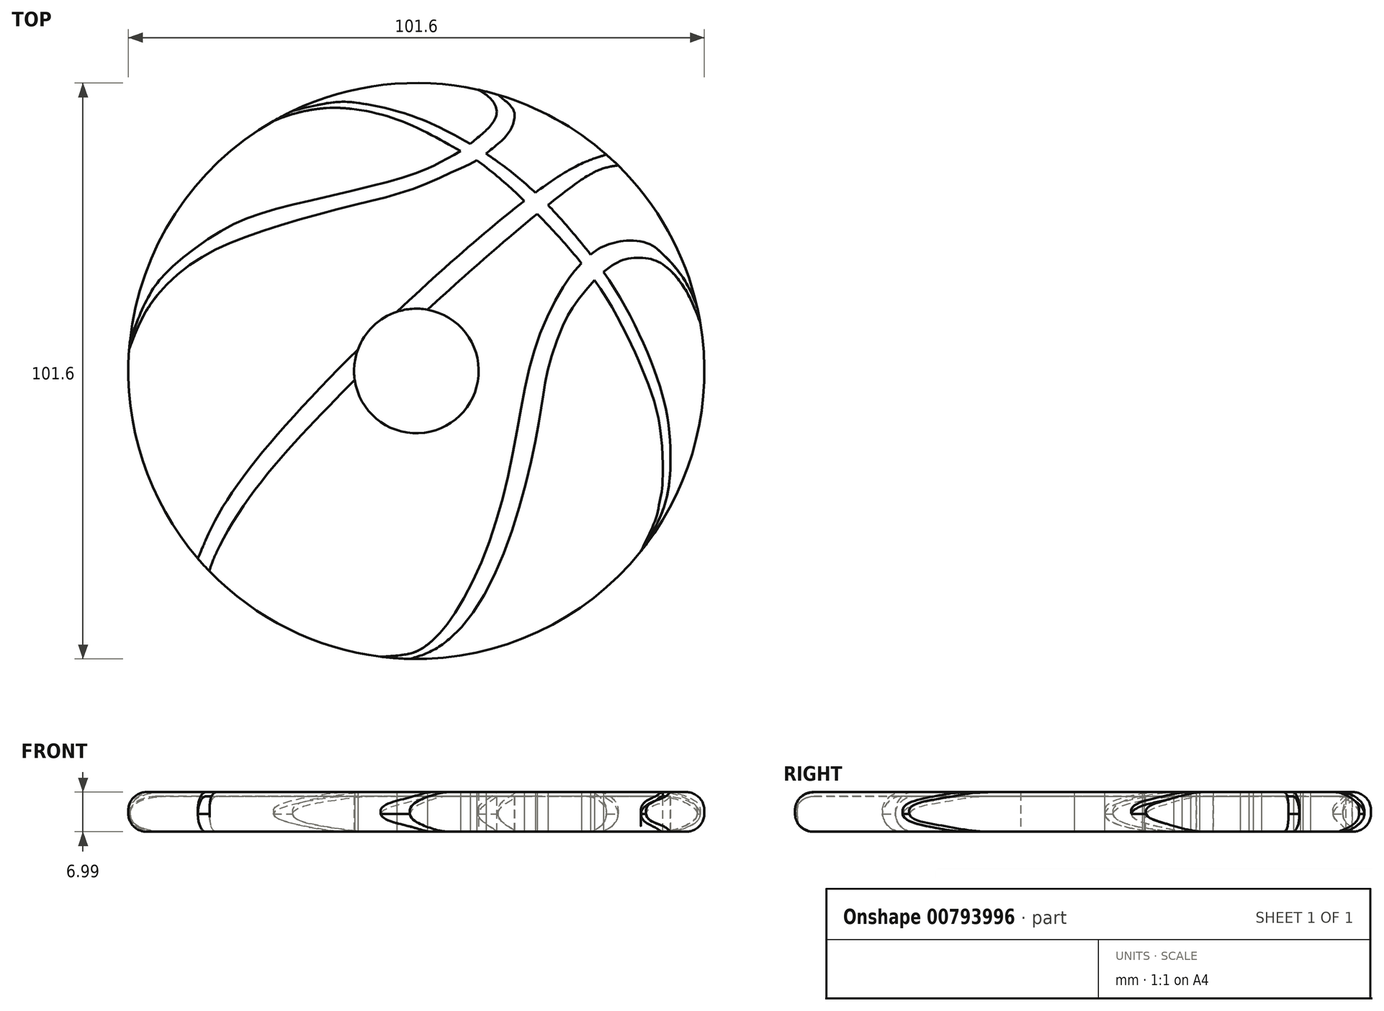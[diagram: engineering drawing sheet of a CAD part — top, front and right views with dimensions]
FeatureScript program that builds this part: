
annotation { "Feature Type Name" : "Feature", "Feature Type Description" : "" }
export const myFeature = defineFeature(function(context is Context, id is Id, definition is map)
    precondition{}
    {
        {
            var Q0;
            Q0=qCreatedBy(makeId("Top.planeOp"),FACE);
            var sketch = newSketch(context, id + "F0", { "sketchPlane" : qUnion([Q0])});
            skCircle(sketch, "E0", {"center": v(0, 0) * mm, "radius": 10.99 * mm});
            skCircle(sketch, "E1", {"center": v(0, 0) * mm, "radius": 50.8 * mm});
            skFitSpline(sketch, "E2", {"points": [v(-38.55, -33.09) * mm, v(-32.94, -22.07) * mm, v(-12.55, 1.56) * mm, v(15.88, 27.48) * mm, v(28.35, 36.2) * mm, v(33.51, 38.18) * mm], "startDerivative": vector(26.52, 63.02) * mm, "endDerivative": vector(44.22, 13.53) * mm});
            skFitSpline(sketch, "E3", {"points": [v(35.58, 36.26) * mm, v(33.47, 35.87) * mm, v(28.86, 33.55) * mm, v(2.6, 11.4) * mm, v(-14.88, -5.64) * mm, v(-31.38, -25.11) * mm, v(-36.45, -35.38) * mm, v(-36.28, -35.56) * mm], "startDerivative": vector(-32.77, -4.24) * mm, "endDerivative": vector(11.2, -3.56) * mm});
            skFitSpline(sketch, "E4", {"points": [v(-50.66, 3.83) * mm, v(-47.23, 11.26) * mm, v(-40.15, 18.58) * mm, v(-29.32, 23.93) * mm, v(-12.42, 28.9) * mm, v(-0.95, 32) * mm, v(6.94, 35.36) * mm, v(10.57, 37.12) * mm, v(12.84, 38.78) * mm, v(15.6, 41.18) * mm, v(16.88, 43.13) * mm, v(17.35, 45.02) * mm, v(16.87, 46.44) * mm, v(14.4, 48.72) * mm], "startDerivative": vector(30.71, 83.36) * mm, "endDerivative": vector(-51.21, 39.87) * mm});
            skFitSpline(sketch, "E5", {"points": [v(10.85, 49.63) * mm, v(12.98, 48.15) * mm, v(14.02, 46.6) * mm, v(14.1, 45.01) * mm, v(12.56, 42.7) * mm, v(9.65, 40.22) * mm, v(7.47, 38.59) * mm, v(4.88, 37.2) * mm, v(2.28, 35.85) * mm, v(-5.69, 33.19) * mm, v(-23.58, 28.89) * mm, v(-33.83, 25.05) * mm, v(-42.81, 18.58) * mm, v(-46.8, 13.9) * mm, v(-49.27, 8.7) * mm, v(-50.53, 5.27) * mm], "startDerivative": vector(49.03, -27.61) * mm, "endDerivative": vector(-19.2, -56.5) * mm});
            skFitSpline(sketch, "E6", {"points": [v(-25.25, 44.08) * mm, v(-21.6, 45.38) * mm, v(-16.31, 46.34) * mm, v(-11.02, 46.2) * mm, v(-4.62, 44.77) * mm, v(1.88, 42.02) * mm, v(6.9, 39.3) * mm, v(11.36, 36.64) * mm, v(16, 32.85) * mm, v(18.05, 30.97) * mm, v(23.06, 25.9) * mm, v(27.84, 20.58) * mm, v(33.1, 13.56) * mm, v(37.68, 5.17) * mm, v(40.4, -1.03) * mm, v(42.45, -7.23) * mm, v(43.42, -14.55) * mm, v(43.34, -20.68) * mm, v(42.78, -23.76) * mm, v(42.38, -25.61) * mm, v(40.73, -29.53) * mm, v(39.6, -31.82) * mm, v(39.61, -31.8) * mm], "startDerivative": vector(85.9, 34.36) * mm, "endDerivative": vector(5.21, 7.59) * mm});
            skFitSpline(sketch, "E7", {"points": [v(40.48, -30.69) * mm, v(41.8, -28.23) * mm, v(43.88, -23.43) * mm, v(44.82, -16.64) * mm, v(44.28, -8.22) * mm, v(41.16, 2.27) * mm, v(33.84, 16.28) * mm, v(27.1, 24.95) * mm, v(23.82, 28.63) * mm, v(16.07, 35.65) * mm, v(4.58, 42.74) * mm, v(-3.48, 45.87) * mm, v(-8.9, 47.06) * mm, v(-15.22, 47.32) * mm, v(-21.87, 45.85) * mm, v(-21.82, 45.87) * mm], "startDerivative": vector(30.28, 53.24) * mm, "endDerivative": vector(13.66, 5.99) * mm});
            skFitSpline(sketch, "E8", {"points": [v(50.08, 8.51) * mm, v(48.7, 11.91) * mm, v(47.22, 14.73) * mm, v(45.05, 17.48) * mm, v(42.78, 19.2) * mm, v(40.3, 19.93) * mm, v(37.19, 19.77) * mm, v(34.29, 18.44) * mm, v(30.3, 14.76) * mm, v(27.7, 11.31) * mm, v(26.2, 8.77) * mm, v(23.46, 1.25) * mm, v(22.42, -3.96) * mm, v(21.18, -11.48) * mm, v(16.87, -28.15) * mm, v(9.65, -43.12) * mm, v(3.23, -49.1) * mm, v(-1.14, -50.79) * mm], "startDerivative": vector(-27.86, 72.87) * mm, "endDerivative": vector(-78.57, -22.07) * mm});
            skFitSpline(sketch, "E9", {"points": [v(-6.28, -50.41) * mm, v(-2.71, -50.13) * mm, v(0.45, -49.27) * mm, v(3.49, -46.92) * mm, v(6.26, -43.54) * mm, v(11.48, -33.71) * mm, v(16.31, -17.9) * mm, v(19.39, -2) * mm, v(22.68, 8.65) * mm, v(26.66, 16.05) * mm, v(28.24, 17.97) * mm, v(31.15, 20.88) * mm, v(33.92, 22.33) * mm, v(37.05, 22.98) * mm, v(41.06, 22.42) * mm, v(43.42, 20.67) * mm, v(45.13, 18.91) * mm, v(47, 16.48) * mm, v(48.5, 13.78) * mm, v(49.58, 11.09) * mm, v(49.6, 10.98) * mm], "startDerivative": vector(83, 3.39) * mm, "endDerivative": vector(1.21, -9.03) * mm});
            skSolve(sketch);
        }
        {
            var Q0;
            {var subQ0=sQuery(id+"F0.wireOp",EDGE,"E4");var subQ1=sQuery(id+"F0.wireOp",EDGE,"E1");var subQ2=makeQuery(id+"F0.imprint","INTERSECT",VERTEX,{"disambiguationData":[OD(0.0)],"derivedFrom":[subQ1,subQ0]});Q0=makeQuery(id+"F0.imprint","IMPRINT",FACE,{"disambiguationData":[TD([[makeQuery(id+"F0.imprint","IMPRINT",EDGE,{"disambiguationData":[TD([[subQ2,1.0]])],"derivedFrom":subQ1}),1.0]])]});}
            var Q1;
            {var subQ0=sQuery(id+"F0.wireOp",EDGE,"E6");var subQ1=sQuery(id+"F0.wireOp",EDGE,"E4");var subQ2=makeQuery(id+"F0.imprint","INTERSECT",VERTEX,{"derivedFrom":[subQ1,subQ0]});Q1=makeQuery(id+"F0.imprint","IMPRINT",FACE,{"disambiguationData":[TD([[makeQuery(id+"F0.imprint","IMPRINT",EDGE,{"disambiguationData":[TD([[subQ2,-1.0]])],"derivedFrom":subQ1}),1.0]])]});}
            var Q2;
            {var subQ0=sQuery(id+"F0.wireOp",EDGE,"E4");var subQ1=sQuery(id+"F0.wireOp",EDGE,"E1");var subQ2=makeQuery(id+"F0.imprint","INTERSECT",VERTEX,{"disambiguationData":[OD(1.0)],"derivedFrom":[subQ1,subQ0]});Q2=makeQuery(id+"F0.imprint","IMPRINT",FACE,{"disambiguationData":[TD([[makeQuery(id+"F0.imprint","IMPRINT",EDGE,{"disambiguationData":[TD([[subQ2,-1.0]])],"derivedFrom":subQ1}),1.0]])]});}
            var Q3;
            {var subQ0=sQuery(id+"F0.wireOp",EDGE,"E6");var subQ1=sQuery(id+"F0.wireOp",EDGE,"E1");var subQ2=makeQuery(id+"F0.imprint","INTERSECT",VERTEX,{"disambiguationData":[OD(0.0)],"derivedFrom":[subQ1,subQ0]});Q3=makeQuery(id+"F0.imprint","IMPRINT",FACE,{"disambiguationData":[TD([[makeQuery(id+"F0.imprint","IMPRINT",EDGE,{"disambiguationData":[TD([[subQ2,1.0]])],"derivedFrom":subQ1}),1.0]])]});}
            var Q4;
            {var subQ0=sQuery(id+"F0.wireOp",EDGE,"E6");var subQ1=sQuery(id+"F0.wireOp",EDGE,"E2");var subQ2=makeQuery(id+"F0.imprint","INTERSECT",VERTEX,{"derivedFrom":[subQ1,subQ0]});Q4=makeQuery(id+"F0.imprint","IMPRINT",FACE,{"disambiguationData":[TD([[makeQuery(id+"F0.imprint","IMPRINT",EDGE,{"disambiguationData":[TD([[subQ2,-1.0]])],"derivedFrom":subQ1}),1.0]])]});}
            var Q5;
            {var subQ0=sQuery(id+"F0.wireOp",EDGE,"E6");var subQ1=sQuery(id+"F0.wireOp",EDGE,"E2");var subQ2=makeQuery(id+"F0.imprint","INTERSECT",VERTEX,{"derivedFrom":[subQ1,subQ0]});Q5=makeQuery(id+"F0.imprint","IMPRINT",FACE,{"disambiguationData":[TD([[makeQuery(id+"F0.imprint","IMPRINT",EDGE,{"disambiguationData":[TD([[subQ2,-1.0]])],"derivedFrom":subQ1}),-1.0]])]});}
            var Q6;
            {var subQ0=sQuery(id+"F0.wireOp",EDGE,"E2");var subQ1=sQuery(id+"F0.wireOp",EDGE,"E1");var subQ2=makeQuery(id+"F0.imprint","INTERSECT",VERTEX,{"disambiguationData":[OD(1.0)],"derivedFrom":[subQ1,subQ0]});Q6=makeQuery(id+"F0.imprint","IMPRINT",FACE,{"disambiguationData":[TD([[makeQuery(id+"F0.imprint","IMPRINT",EDGE,{"disambiguationData":[TD([[subQ2,1.0]])],"derivedFrom":subQ1}),1.0]])]});}
            var Q7;
            {var subQ0=sQuery(id+"F0.wireOp",EDGE,"E2");var subQ1=sQuery(id+"F0.wireOp",EDGE,"E0");var subQ2=makeQuery(id+"F0.imprint","INTERSECT",VERTEX,{"disambiguationData":[OD(0.0)],"derivedFrom":[subQ1,subQ0]});Q7=makeQuery(id+"F0.imprint","IMPRINT",FACE,{"disambiguationData":[TD([[makeQuery(id+"F0.imprint","IMPRINT",EDGE,{"disambiguationData":[TD([[subQ2,1.0]])],"derivedFrom":subQ1}),-1.0]])]});}
            var Q8;
            {var subQ0=sQuery(id+"F0.wireOp",EDGE,"E2");var subQ1=sQuery(id+"F0.wireOp",EDGE,"E0");var subQ2=makeQuery(id+"F0.imprint","INTERSECT",VERTEX,{"disambiguationData":[OD(1.0)],"derivedFrom":[subQ1,subQ0]});Q8=makeQuery(id+"F0.imprint","IMPRINT",FACE,{"disambiguationData":[TD([[makeQuery(id+"F0.imprint","IMPRINT",EDGE,{"disambiguationData":[TD([[subQ2,-1.0]])],"derivedFrom":subQ1}),-1.0]])]});}
            var Q9;
            {var subQ0=sQuery(id+"F0.wireOp",EDGE,"E8");var subQ1=sQuery(id+"F0.wireOp",EDGE,"E1");var subQ2=makeQuery(id+"F0.imprint","INTERSECT",VERTEX,{"disambiguationData":[OD(1.0)],"derivedFrom":[subQ1,subQ0]});Q9=makeQuery(id+"F0.imprint","IMPRINT",FACE,{"disambiguationData":[TD([[makeQuery(id+"F0.imprint","IMPRINT",EDGE,{"disambiguationData":[TD([[subQ2,1.0]])],"derivedFrom":subQ1}),1.0]])]});}
            var Q10;
            {var subQ0=sQuery(id+"F0.wireOp",EDGE,"E7");var subQ1=sQuery(id+"F0.wireOp",EDGE,"E3");var subQ2=makeQuery(id+"F0.imprint","INTERSECT",VERTEX,{"derivedFrom":[subQ1,subQ0]});Q10=makeQuery(id+"F0.imprint","IMPRINT",FACE,{"disambiguationData":[TD([[makeQuery(id+"F0.imprint","IMPRINT",EDGE,{"disambiguationData":[TD([[subQ2,-1.0]])],"derivedFrom":subQ1}),1.0]])]});}
            var Q11;
            {var subQ0=sQuery(id+"F0.wireOp",EDGE,"E9");var subQ1=sQuery(id+"F0.wireOp",EDGE,"E6");var subQ2=makeQuery(id+"F0.imprint","INTERSECT",VERTEX,{"derivedFrom":[subQ1,subQ0]});Q11=makeQuery(id+"F0.imprint","IMPRINT",FACE,{"disambiguationData":[TD([[makeQuery(id+"F0.imprint","IMPRINT",EDGE,{"disambiguationData":[TD([[subQ2,-1.0]])],"derivedFrom":subQ1}),1.0]])]});}
            var Q12;
            {var subQ0=sQuery(id+"F0.wireOp",EDGE,"E8");var subQ1=sQuery(id+"F0.wireOp",EDGE,"E1");var subQ2=makeQuery(id+"F0.imprint","INTERSECT",VERTEX,{"disambiguationData":[OD(0.0)],"derivedFrom":[subQ1,subQ0]});Q12=makeQuery(id+"F0.imprint","IMPRINT",FACE,{"disambiguationData":[TD([[makeQuery(id+"F0.imprint","IMPRINT",EDGE,{"disambiguationData":[TD([[subQ2,-1.0]])],"derivedFrom":subQ1}),1.0]])]});}
            var Q13;
            {var subQ1=sQuery(id+"F0.wireOp",EDGE,"E1");var subQ5=sQuery(id+"F0.wireOp",EDGE,"E6");var subQ8=makeQuery(id+"F0.imprint","INTERSECT",VERTEX,{"disambiguationData":[OD(1.0)],"derivedFrom":[subQ1,subQ5]});Q13=makeQuery(id+"F0.imprint","IMPRINT",FACE,{"disambiguationData":[TD([[makeQuery(id+"F0.imprint","IMPRINT",EDGE,{"disambiguationData":[TD([[subQ8,1.0]])],"derivedFrom":subQ1}),1.0]])]});}
            extrude(context, id + "F1", {"entities" : qUnion([Q0, Q1, Q2, Q3, Q4, Q5, Q6, Q7, Q8, Q9, Q10, Q11, Q12, Q13]), "depth" : 6.22 * mm, "offsetDistance" : 25.4 * mm});
        }
        {
            var Q0;
            {var subQ0=sQuery(id+"F0.wireOp",EDGE,"E5");var subQ1=sQuery(id+"F0.wireOp",EDGE,"E1");var subQ2=makeQuery(id+"F0.imprint","INTERSECT",VERTEX,{"disambiguationData":[OD(1.0)],"derivedFrom":[subQ1,subQ0]});Q0=makeQuery(id+"F0.imprint","IMPRINT",FACE,{"disambiguationData":[TD([[makeQuery(id+"F0.imprint","IMPRINT",EDGE,{"disambiguationData":[TD([[subQ2,1.0]])],"derivedFrom":subQ1}),1.0]])]});}
            var Q1;
            {var subQ0=sQuery(id+"F0.wireOp",EDGE,"E2");var subQ3=sQuery(id+"F0.wireOp",EDGE,"E0");var subQ9=makeQuery(id+"F0.imprint","INTERSECT",VERTEX,{"disambiguationData":[OD(0.0)],"derivedFrom":[subQ3,subQ0]});Q1=makeQuery(id+"F0.imprint","IMPRINT",FACE,{"disambiguationData":[TD([[makeQuery(id+"F0.imprint","IMPRINT",EDGE,{"disambiguationData":[TD([[subQ9,-1.0]])],"derivedFrom":subQ3}),-1.0]])]});}
            var Q2;
            {var subQ0=sQuery(id+"F0.wireOp",EDGE,"E2");var subQ1=sQuery(id+"F0.wireOp",EDGE,"E1");var subQ2=makeQuery(id+"F0.imprint","INTERSECT",VERTEX,{"disambiguationData":[OD(1.0)],"derivedFrom":[subQ1,subQ0]});Q2=makeQuery(id+"F0.imprint","IMPRINT",FACE,{"disambiguationData":[TD([[makeQuery(id+"F0.imprint","IMPRINT",EDGE,{"disambiguationData":[TD([[subQ2,-1.0]])],"derivedFrom":subQ1}),1.0]])]});}
            var Q3;
            {var subQ0=sQuery(id+"F0.wireOp",EDGE,"E5");var subQ1=sQuery(id+"F0.wireOp",EDGE,"E1");var subQ2=makeQuery(id+"F0.imprint","INTERSECT",VERTEX,{"disambiguationData":[OD(0.0)],"derivedFrom":[subQ1,subQ0]});Q3=makeQuery(id+"F0.imprint","IMPRINT",FACE,{"disambiguationData":[TD([[makeQuery(id+"F0.imprint","IMPRINT",EDGE,{"disambiguationData":[TD([[subQ2,-1.0]])],"derivedFrom":subQ1}),1.0]])]});}
            var Q4;
            {var subQ0=sQuery(id+"F0.wireOp",EDGE,"E3");var subQ1=sQuery(id+"F0.wireOp",EDGE,"E0");var subQ2=makeQuery(id+"F0.imprint","INTERSECT",VERTEX,{"disambiguationData":[OD(0.0)],"derivedFrom":[subQ1,subQ0]});Q4=makeQuery(id+"F0.imprint","IMPRINT",FACE,{"disambiguationData":[TD([[makeQuery(id+"F0.imprint","IMPRINT",EDGE,{"disambiguationData":[TD([[subQ2,1.0]])],"derivedFrom":subQ1}),-1.0]])]});}
            var Q5;
            {var subQ0=sQuery(id+"F0.wireOp",EDGE,"E3");var subQ1=sQuery(id+"F0.wireOp",EDGE,"E1");var subQ2=makeQuery(id+"F0.imprint","INTERSECT",VERTEX,{"disambiguationData":[OD(0.0)],"derivedFrom":[subQ1,subQ0]});Q5=makeQuery(id+"F0.imprint","IMPRINT",FACE,{"disambiguationData":[TD([[makeQuery(id+"F0.imprint","IMPRINT",EDGE,{"disambiguationData":[TD([[subQ2,1.0]])],"derivedFrom":subQ1}),1.0]])]});}
            var Q6;
            {var subQ0=sQuery(id+"F0.wireOp",EDGE,"E8");var subQ1=sQuery(id+"F0.wireOp",EDGE,"E1");var subQ2=makeQuery(id+"F0.imprint","INTERSECT",VERTEX,{"disambiguationData":[OD(1.0)],"derivedFrom":[subQ1,subQ0]});Q6=makeQuery(id+"F0.imprint","IMPRINT",FACE,{"disambiguationData":[TD([[makeQuery(id+"F0.imprint","IMPRINT",EDGE,{"disambiguationData":[TD([[subQ2,-1.0]])],"derivedFrom":subQ1}),1.0]])]});}
            var Q7;
            {var subQ0=sQuery(id+"F0.wireOp",EDGE,"E7");var subQ1=sQuery(id+"F0.wireOp",EDGE,"E1");var subQ2=makeQuery(id+"F0.imprint","INTERSECT",VERTEX,{"disambiguationData":[OD(0.0)],"derivedFrom":[subQ1,subQ0]});Q7=makeQuery(id+"F0.imprint","IMPRINT",FACE,{"disambiguationData":[TD([[makeQuery(id+"F0.imprint","IMPRINT",EDGE,{"disambiguationData":[TD([[subQ2,-1.0]])],"derivedFrom":subQ1}),1.0]])]});}
            extrude(context, id + "F2", {"entities" : qUnion([Q0, Q1, Q2, Q3, Q4, Q5, Q6, Q7]), "depth" : 7 * mm, "offsetDistance" : 25.4 * mm});
        }
        {
            var Q0;
            {var subQ0=sQuery(id+"F0.wireOp",EDGE,"E1");Q0=makeQuery(id+"F2.opExtrude","CAP_EDGE",EDGE,{"disambiguationData":[OSD([subQ0]),TDD([makeQuery(id+"F0.imprint","IMPRINT",EDGE,{"disambiguationData":[TD([[makeQuery(id+"F0.imprint","INTERSECT",VERTEX,{"disambiguationData":[OD(1.0)],"derivedFrom":[subQ0,sQuery(id+"F0.wireOp",EDGE,"E5")]}),1.0]])],"derivedFrom":subQ0})])],"isStart":false});}
            var Q1;
            {var subQ0=sQuery(id+"F0.wireOp",EDGE,"E1");Q1=makeQuery(id+"F2.opExtrude","CAP_EDGE",EDGE,{"disambiguationData":[OSD([subQ0]),TDD([makeQuery(id+"F0.imprint","IMPRINT",EDGE,{"disambiguationData":[TD([[makeQuery(id+"F0.imprint","INTERSECT",VERTEX,{"disambiguationData":[OD(0.0)],"derivedFrom":[subQ0,sQuery(id+"F0.wireOp",EDGE,"E2")]}),1.0]])],"derivedFrom":subQ0})])],"isStart":false});}
            var Q2;
            {var subQ0=sQuery(id+"F0.wireOp",EDGE,"E3");var subQ1=sQuery(id+"F0.wireOp",EDGE,"E1");var subQ2=makeQuery(id+"F0.imprint","INTERSECT",VERTEX,{"disambiguationData":[OD(1.0)],"derivedFrom":[subQ1,subQ0]});Q2=makeQuery(id+"F2.opExtrude","CAP_EDGE",EDGE,{"disambiguationData":[OSD([subQ1]),TDD([makeQuery(id+"F0.imprint","IMPRINT",EDGE,{"disambiguationData":[TD([[subQ2,1.0]])],"derivedFrom":subQ1}),makeQuery(id+"F0.imprint","IMPRINT",EDGE,{"disambiguationData":[TD([[subQ2,-1.0]])],"derivedFrom":subQ1})])],"isStart":false});}
            var Q3;
            {var subQ0=sQuery(id+"F0.wireOp",EDGE,"E1");Q3=makeQuery(id+"F1.opExtrude","CAP_EDGE",EDGE,{"disambiguationData":[OSD([subQ0]),TDD([makeQuery(id+"F0.imprint","IMPRINT",EDGE,{"disambiguationData":[TD([[makeQuery(id+"F0.imprint","INTERSECT",VERTEX,{"disambiguationData":[OD(0.0)],"derivedFrom":[subQ0,sQuery(id+"F0.wireOp",EDGE,"E2")]}),-1.0]])],"derivedFrom":subQ0})])],"isStart":false});}
            var Q4;
            {var subQ0=sQuery(id+"F0.wireOp",EDGE,"E1");Q4=makeQuery(id+"F1.opExtrude","CAP_EDGE",EDGE,{"disambiguationData":[OSD([subQ0]),TDD([makeQuery(id+"F0.imprint","IMPRINT",EDGE,{"disambiguationData":[TD([[makeQuery(id+"F0.imprint","INTERSECT",VERTEX,{"disambiguationData":[OD(0.0)],"derivedFrom":[subQ0,sQuery(id+"F0.wireOp",EDGE,"E4")]}),1.0]])],"derivedFrom":subQ0})])],"isStart":false});}
            var Q5;
            {var subQ0=sQuery(id+"F0.wireOp",EDGE,"E1");Q5=makeQuery(id+"F1.opExtrude","CAP_EDGE",EDGE,{"disambiguationData":[OSD([subQ0]),TDD([makeQuery(id+"F0.imprint","IMPRINT",EDGE,{"disambiguationData":[TD([[makeQuery(id+"F0.imprint","INTERSECT",VERTEX,{"disambiguationData":[OD(1.0)],"derivedFrom":[subQ0,sQuery(id+"F0.wireOp",EDGE,"E8")]}),1.0]])],"derivedFrom":subQ0})])],"isStart":false});}
            var Q6;
            {var subQ0=sQuery(id+"F0.wireOp",EDGE,"E1");Q6=makeQuery(id+"F2.opExtrude","CAP_EDGE",EDGE,{"disambiguationData":[OSD([subQ0]),TDD([makeQuery(id+"F0.imprint","IMPRINT",EDGE,{"disambiguationData":[TD([[makeQuery(id+"F0.imprint","INTERSECT",VERTEX,{"disambiguationData":[OD(1.0)],"derivedFrom":[subQ0,sQuery(id+"F0.wireOp",EDGE,"E8")]}),-1.0]])],"derivedFrom":subQ0})])],"isStart":false});}
            var Q7;
            {var subQ0=sQuery(id+"F0.wireOp",EDGE,"E1");Q7=makeQuery(id+"F2.opExtrude","CAP_EDGE",EDGE,{"disambiguationData":[OSD([subQ0]),TDD([makeQuery(id+"F0.imprint","IMPRINT",EDGE,{"disambiguationData":[TD([[makeQuery(id+"F0.imprint","INTERSECT",VERTEX,{"disambiguationData":[OD(0.0)],"derivedFrom":[subQ0,sQuery(id+"F0.wireOp",EDGE,"E7")]}),-1.0]])],"derivedFrom":subQ0})])],"isStart":false});}
            var Q8;
            {var subQ0=sQuery(id+"F0.wireOp",EDGE,"E6");var subQ1=sQuery(id+"F0.wireOp",EDGE,"E1");var subQ2=makeQuery(id+"F0.imprint","INTERSECT",VERTEX,{"disambiguationData":[OD(1.0)],"derivedFrom":[subQ1,subQ0]});Q8=makeQuery(id+"F1.opExtrude","CAP_EDGE",EDGE,{"disambiguationData":[OSD([subQ1]),TDD([makeQuery(id+"F0.imprint","IMPRINT",EDGE,{"disambiguationData":[TD([[subQ2,1.0]])],"derivedFrom":subQ1}),makeQuery(id+"F0.imprint","IMPRINT",EDGE,{"disambiguationData":[TD([[subQ2,-1.0]])],"derivedFrom":subQ1})])],"isStart":false});}
            var Q9;
            {var subQ0=sQuery(id+"F0.wireOp",EDGE,"E9");var subQ1=sQuery(id+"F0.wireOp",EDGE,"E1");var subQ2=makeQuery(id+"F0.imprint","INTERSECT",VERTEX,{"disambiguationData":[OD(1.0)],"derivedFrom":[subQ1,subQ0]});Q9=makeQuery(id+"F1.opExtrude","CAP_EDGE",EDGE,{"disambiguationData":[OSD([subQ1]),TDD([makeQuery(id+"F0.imprint","IMPRINT",EDGE,{"disambiguationData":[TD([[makeQuery(id+"F0.imprint","INTERSECT",VERTEX,{"disambiguationData":[OD(0.0)],"derivedFrom":[subQ1,sQuery(id+"F0.wireOp",EDGE,"E8")]}),-1.0]])],"derivedFrom":subQ1}),makeQuery(id+"F0.imprint","IMPRINT",EDGE,{"disambiguationData":[TD([[subQ2,-1.0]])],"derivedFrom":subQ1})])],"isStart":false});}
            var Q10;
            {var subQ0=sQuery(id+"F0.wireOp",EDGE,"E1");Q10=makeQuery(id+"F2.opExtrude","CAP_EDGE",EDGE,{"disambiguationData":[OSD([subQ0]),TDD([makeQuery(id+"F0.imprint","IMPRINT",EDGE,{"disambiguationData":[TD([[makeQuery(id+"F0.imprint","INTERSECT",VERTEX,{"disambiguationData":[OD(0.0)],"derivedFrom":[subQ0,sQuery(id+"F0.wireOp",EDGE,"E3")]}),1.0]])],"derivedFrom":subQ0})])],"isStart":false});}
            var Q11;
            {var subQ0=sQuery(id+"F0.wireOp",EDGE,"E1");Q11=makeQuery(id+"F1.opExtrude","CAP_EDGE",EDGE,{"disambiguationData":[OSD([subQ0]),TDD([makeQuery(id+"F0.imprint","IMPRINT",EDGE,{"disambiguationData":[TD([[makeQuery(id+"F0.imprint","INTERSECT",VERTEX,{"disambiguationData":[OD(1.0)],"derivedFrom":[subQ0,sQuery(id+"F0.wireOp",EDGE,"E2")]}),1.0]])],"derivedFrom":subQ0})])],"isStart":false});}
            var Q12;
            {var subQ0=sQuery(id+"F0.wireOp",EDGE,"E1");Q12=makeQuery(id+"F2.opExtrude","CAP_EDGE",EDGE,{"disambiguationData":[OSD([subQ0]),TDD([makeQuery(id+"F0.imprint","IMPRINT",EDGE,{"disambiguationData":[TD([[makeQuery(id+"F0.imprint","INTERSECT",VERTEX,{"disambiguationData":[OD(1.0)],"derivedFrom":[subQ0,sQuery(id+"F0.wireOp",EDGE,"E2")]}),-1.0]])],"derivedFrom":subQ0})])],"isStart":false});}
            var Q13;
            {var subQ0=sQuery(id+"F0.wireOp",EDGE,"E1");Q13=makeQuery(id+"F1.opExtrude","CAP_EDGE",EDGE,{"disambiguationData":[OSD([subQ0]),TDD([makeQuery(id+"F0.imprint","IMPRINT",EDGE,{"disambiguationData":[TD([[makeQuery(id+"F0.imprint","INTERSECT",VERTEX,{"disambiguationData":[OD(1.0)],"derivedFrom":[subQ0,sQuery(id+"F0.wireOp",EDGE,"E4")]}),-1.0]])],"derivedFrom":subQ0})])],"isStart":false});}
            var Q14;
            {var subQ0=sQuery(id+"F0.wireOp",EDGE,"E7");var subQ1=sQuery(id+"F0.wireOp",EDGE,"E1");var subQ2=makeQuery(id+"F0.imprint","INTERSECT",VERTEX,{"disambiguationData":[OD(1.0)],"derivedFrom":[subQ1,subQ0]});Q14=makeQuery(id+"F2.opExtrude","CAP_EDGE",EDGE,{"disambiguationData":[OSD([subQ1]),TDD([makeQuery(id+"F0.imprint","IMPRINT",EDGE,{"disambiguationData":[TD([[makeQuery(id+"F0.imprint","INTERSECT",VERTEX,{"disambiguationData":[OD(0.0)],"derivedFrom":[subQ1,sQuery(id+"F0.wireOp",EDGE,"E5")]}),-1.0]])],"derivedFrom":subQ1}),makeQuery(id+"F0.imprint","IMPRINT",EDGE,{"disambiguationData":[TD([[subQ2,-1.0]])],"derivedFrom":subQ1})])],"isStart":false});}
            var Q15;
            {var subQ0=sQuery(id+"F0.wireOp",EDGE,"E1");Q15=makeQuery(id+"F1.opExtrude","CAP_EDGE",EDGE,{"disambiguationData":[OSD([subQ0]),TDD([makeQuery(id+"F0.imprint","IMPRINT",EDGE,{"disambiguationData":[TD([[makeQuery(id+"F0.imprint","INTERSECT",VERTEX,{"disambiguationData":[OD(0.0)],"derivedFrom":[subQ0,sQuery(id+"F0.wireOp",EDGE,"E6")]}),1.0]])],"derivedFrom":subQ0})])],"isStart":false});}
            var Q16;
            {var subQ0=sQuery(id+"F0.wireOp",EDGE,"E7");var subQ1=sQuery(id+"F0.wireOp",EDGE,"E1");var subQ2=makeQuery(id+"F0.imprint","INTERSECT",VERTEX,{"disambiguationData":[OD(1.0)],"derivedFrom":[subQ1,subQ0]});Q16=makeQuery(id+"F2.opExtrude","CAP_EDGE",EDGE,{"disambiguationData":[OSD([subQ1]),TDD([makeQuery(id+"F0.imprint","IMPRINT",EDGE,{"disambiguationData":[TD([[makeQuery(id+"F0.imprint","INTERSECT",VERTEX,{"disambiguationData":[OD(0.0)],"derivedFrom":[subQ1,sQuery(id+"F0.wireOp",EDGE,"E5")]}),-1.0]])],"derivedFrom":subQ1}),makeQuery(id+"F0.imprint","IMPRINT",EDGE,{"disambiguationData":[TD([[subQ2,-1.0]])],"derivedFrom":subQ1})])],"isStart":true});}
            var Q17;
            {var subQ0=sQuery(id+"F0.wireOp",EDGE,"E1");Q17=makeQuery(id+"F1.opExtrude","CAP_EDGE",EDGE,{"disambiguationData":[OSD([subQ0]),TDD([makeQuery(id+"F0.imprint","IMPRINT",EDGE,{"disambiguationData":[TD([[makeQuery(id+"F0.imprint","INTERSECT",VERTEX,{"disambiguationData":[OD(1.0)],"derivedFrom":[subQ0,sQuery(id+"F0.wireOp",EDGE,"E4")]}),-1.0]])],"derivedFrom":subQ0})])],"isStart":true});}
            var Q18;
            {var subQ0=sQuery(id+"F0.wireOp",EDGE,"E1");Q18=makeQuery(id+"F2.opExtrude","CAP_EDGE",EDGE,{"disambiguationData":[OSD([subQ0]),TDD([makeQuery(id+"F0.imprint","IMPRINT",EDGE,{"disambiguationData":[TD([[makeQuery(id+"F0.imprint","INTERSECT",VERTEX,{"disambiguationData":[OD(1.0)],"derivedFrom":[subQ0,sQuery(id+"F0.wireOp",EDGE,"E2")]}),-1.0]])],"derivedFrom":subQ0})])],"isStart":true});}
            var Q19;
            {var subQ0=sQuery(id+"F0.wireOp",EDGE,"E1");Q19=makeQuery(id+"F1.opExtrude","CAP_EDGE",EDGE,{"disambiguationData":[OSD([subQ0]),TDD([makeQuery(id+"F0.imprint","IMPRINT",EDGE,{"disambiguationData":[TD([[makeQuery(id+"F0.imprint","INTERSECT",VERTEX,{"disambiguationData":[OD(0.0)],"derivedFrom":[subQ0,sQuery(id+"F0.wireOp",EDGE,"E6")]}),1.0]])],"derivedFrom":subQ0})])],"isStart":true});}
            var Q20;
            {var subQ0=sQuery(id+"F0.wireOp",EDGE,"E1");Q20=makeQuery(id+"F2.opExtrude","CAP_EDGE",EDGE,{"disambiguationData":[OSD([subQ0]),TDD([makeQuery(id+"F0.imprint","IMPRINT",EDGE,{"disambiguationData":[TD([[makeQuery(id+"F0.imprint","INTERSECT",VERTEX,{"disambiguationData":[OD(1.0)],"derivedFrom":[subQ0,sQuery(id+"F0.wireOp",EDGE,"E5")]}),1.0]])],"derivedFrom":subQ0})])],"isStart":true});}
            var Q21;
            {var subQ0=sQuery(id+"F0.wireOp",EDGE,"E1");Q21=makeQuery(id+"F1.opExtrude","CAP_EDGE",EDGE,{"disambiguationData":[OSD([subQ0]),TDD([makeQuery(id+"F0.imprint","IMPRINT",EDGE,{"disambiguationData":[TD([[makeQuery(id+"F0.imprint","INTERSECT",VERTEX,{"disambiguationData":[OD(0.0)],"derivedFrom":[subQ0,sQuery(id+"F0.wireOp",EDGE,"E4")]}),1.0]])],"derivedFrom":subQ0})])],"isStart":true});}
            var Q22;
            {var subQ0=sQuery(id+"F0.wireOp",EDGE,"E1");Q22=makeQuery(id+"F2.opExtrude","CAP_EDGE",EDGE,{"disambiguationData":[OSD([subQ0]),TDD([makeQuery(id+"F0.imprint","IMPRINT",EDGE,{"disambiguationData":[TD([[makeQuery(id+"F0.imprint","INTERSECT",VERTEX,{"disambiguationData":[OD(0.0)],"derivedFrom":[subQ0,sQuery(id+"F0.wireOp",EDGE,"E2")]}),1.0]])],"derivedFrom":subQ0})])],"isStart":true});}
            var Q23;
            {var subQ0=sQuery(id+"F0.wireOp",EDGE,"E1");Q23=makeQuery(id+"F1.opExtrude","CAP_EDGE",EDGE,{"disambiguationData":[OSD([subQ0]),TDD([makeQuery(id+"F0.imprint","IMPRINT",EDGE,{"disambiguationData":[TD([[makeQuery(id+"F0.imprint","INTERSECT",VERTEX,{"disambiguationData":[OD(0.0)],"derivedFrom":[subQ0,sQuery(id+"F0.wireOp",EDGE,"E2")]}),-1.0]])],"derivedFrom":subQ0})])],"isStart":true});}
            var Q24;
            {var subQ0=sQuery(id+"F0.wireOp",EDGE,"E3");var subQ1=sQuery(id+"F0.wireOp",EDGE,"E1");var subQ2=makeQuery(id+"F0.imprint","INTERSECT",VERTEX,{"disambiguationData":[OD(1.0)],"derivedFrom":[subQ1,subQ0]});Q24=makeQuery(id+"F2.opExtrude","CAP_EDGE",EDGE,{"disambiguationData":[OSD([subQ1]),TDD([makeQuery(id+"F0.imprint","IMPRINT",EDGE,{"disambiguationData":[TD([[subQ2,1.0]])],"derivedFrom":subQ1}),makeQuery(id+"F0.imprint","IMPRINT",EDGE,{"disambiguationData":[TD([[subQ2,-1.0]])],"derivedFrom":subQ1})])],"isStart":true});}
            var Q25;
            {var subQ0=sQuery(id+"F0.wireOp",EDGE,"E1");Q25=makeQuery(id+"F1.opExtrude","CAP_EDGE",EDGE,{"disambiguationData":[OSD([subQ0]),TDD([makeQuery(id+"F0.imprint","IMPRINT",EDGE,{"disambiguationData":[TD([[makeQuery(id+"F0.imprint","INTERSECT",VERTEX,{"disambiguationData":[OD(1.0)],"derivedFrom":[subQ0,sQuery(id+"F0.wireOp",EDGE,"E8")]}),1.0]])],"derivedFrom":subQ0})])],"isStart":true});}
            var Q26;
            {var subQ0=sQuery(id+"F0.wireOp",EDGE,"E1");Q26=makeQuery(id+"F2.opExtrude","CAP_EDGE",EDGE,{"disambiguationData":[OSD([subQ0]),TDD([makeQuery(id+"F0.imprint","IMPRINT",EDGE,{"disambiguationData":[TD([[makeQuery(id+"F0.imprint","INTERSECT",VERTEX,{"disambiguationData":[OD(1.0)],"derivedFrom":[subQ0,sQuery(id+"F0.wireOp",EDGE,"E8")]}),-1.0]])],"derivedFrom":subQ0})])],"isStart":true});}
            var Q27;
            {var subQ0=sQuery(id+"F0.wireOp",EDGE,"E6");var subQ1=sQuery(id+"F0.wireOp",EDGE,"E1");var subQ2=makeQuery(id+"F0.imprint","INTERSECT",VERTEX,{"disambiguationData":[OD(1.0)],"derivedFrom":[subQ1,subQ0]});Q27=makeQuery(id+"F1.opExtrude","CAP_EDGE",EDGE,{"disambiguationData":[OSD([subQ1]),TDD([makeQuery(id+"F0.imprint","IMPRINT",EDGE,{"disambiguationData":[TD([[subQ2,1.0]])],"derivedFrom":subQ1}),makeQuery(id+"F0.imprint","IMPRINT",EDGE,{"disambiguationData":[TD([[subQ2,-1.0]])],"derivedFrom":subQ1})])],"isStart":true});}
            var Q28;
            {var subQ0=sQuery(id+"F0.wireOp",EDGE,"E1");Q28=makeQuery(id+"F2.opExtrude","CAP_EDGE",EDGE,{"disambiguationData":[OSD([subQ0]),TDD([makeQuery(id+"F0.imprint","IMPRINT",EDGE,{"disambiguationData":[TD([[makeQuery(id+"F0.imprint","INTERSECT",VERTEX,{"disambiguationData":[OD(0.0)],"derivedFrom":[subQ0,sQuery(id+"F0.wireOp",EDGE,"E7")]}),-1.0]])],"derivedFrom":subQ0})])],"isStart":true});}
            var Q29;
            {var subQ0=sQuery(id+"F0.wireOp",EDGE,"E9");var subQ1=sQuery(id+"F0.wireOp",EDGE,"E1");var subQ2=makeQuery(id+"F0.imprint","INTERSECT",VERTEX,{"disambiguationData":[OD(1.0)],"derivedFrom":[subQ1,subQ0]});Q29=makeQuery(id+"F1.opExtrude","CAP_EDGE",EDGE,{"disambiguationData":[OSD([subQ1]),TDD([makeQuery(id+"F0.imprint","IMPRINT",EDGE,{"disambiguationData":[TD([[makeQuery(id+"F0.imprint","INTERSECT",VERTEX,{"disambiguationData":[OD(0.0)],"derivedFrom":[subQ1,sQuery(id+"F0.wireOp",EDGE,"E8")]}),-1.0]])],"derivedFrom":subQ1}),makeQuery(id+"F0.imprint","IMPRINT",EDGE,{"disambiguationData":[TD([[subQ2,-1.0]])],"derivedFrom":subQ1})])],"isStart":true});}
            var Q30;
            {var subQ0=sQuery(id+"F0.wireOp",EDGE,"E1");Q30=makeQuery(id+"F2.opExtrude","CAP_EDGE",EDGE,{"disambiguationData":[OSD([subQ0]),TDD([makeQuery(id+"F0.imprint","IMPRINT",EDGE,{"disambiguationData":[TD([[makeQuery(id+"F0.imprint","INTERSECT",VERTEX,{"disambiguationData":[OD(0.0)],"derivedFrom":[subQ0,sQuery(id+"F0.wireOp",EDGE,"E3")]}),1.0]])],"derivedFrom":subQ0})])],"isStart":true});}
            var Q31;
            {var subQ0=sQuery(id+"F0.wireOp",EDGE,"E1");Q31=makeQuery(id+"F1.opExtrude","CAP_EDGE",EDGE,{"disambiguationData":[OSD([subQ0]),TDD([makeQuery(id+"F0.imprint","IMPRINT",EDGE,{"disambiguationData":[TD([[makeQuery(id+"F0.imprint","INTERSECT",VERTEX,{"disambiguationData":[OD(1.0)],"derivedFrom":[subQ0,sQuery(id+"F0.wireOp",EDGE,"E2")]}),1.0]])],"derivedFrom":subQ0})])],"isStart":true});}
            fillet(context, id + "F3", {"entities" : qUnion([Q0, Q1, Q2, Q3, Q4, Q5, Q6, Q7, Q8, Q9, Q10, Q11, Q12, Q13, Q14, Q15, Q16, Q17, Q18, Q19, Q20, Q21, Q22, Q23, Q24, Q25, Q26, Q27, Q28, Q29, Q30, Q31]), "radius" : 3.17 * mm, "tangentPropagation" : true, "allowEdgeOverflow" : false});
        }
    });
